# Revit family: Sanitary_Showers_hansgrohe_27112400-Raindance-E-Showerpipe-360-1jet_
name_source: partatom
category: Plumbing Fixtures
revit_build: Autodesk Revit 2015 (Build: 20140903_1530(x64)
units: mm (PartAtom-declared; Revit-internal decimal feet)

## types (1)
- white/chrome
    BIMobject category = Showers
    BIMobject category code = sanitary-showers
    BIMobject main category = Sanitary
    BIMobject main category code = sanitary
    Brand url = http://www.hansgrohe-int.com
    Default Elevation = 4' - 0"
    Design country = Germany
    Edition number = 1
    GTIN code = https://4011097679556
    IFC Classification = Sanitary Terminal
    Manufacturer country = Germany
    Manufacturer name = hansgrohe
    Material main = Chrome
    Product Guid = 807001ec-f9b5-4c9b-b449-031a493a514c
    Product SKU = 27112400
    Product data url = https://bimobject.com
    Product family = Raindance E
    Product group = Showerpipes with thermostat
    Product name = 27112400 Raindance E Showerpipe 360 1jet with thermostat
    QR code = http://bimobject.com

## geometry (parser evidence)
native form markers: Sweep x4
no freeform markers — native parametric forms only
